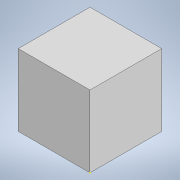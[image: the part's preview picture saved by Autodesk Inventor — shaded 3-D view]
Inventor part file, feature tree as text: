
AUTODESK INVENTOR PART (.ipt)
format: ipt  version: 2021 (Build 250183000, 183)  size: 107,520 bytes
history: native  units: in
note: dims shown in document units (in); Inventor stores cm internally (conversion verified against a paired STEP export)
features: sketch x3, extrude x2
ambient origin geometry x8: Origin, YZ Plane, XZ Plane, XY Plane, X Axis, Y Axis, Z Axis, Center Point
bodies: Solid1 (feature_tree)
feature tree (5):
  sketch  "Sketch1"  dims[d1=0.6299in d2=0.6299in]
  extrude  "Extrusion1"  Depth=0.6299in
  extrude  "Extrusion2"  Depth=0.5118in TaperAngle=0.0deg
  sketch  "Sketch2"  dims[d8=0.6299in d9=0.0in d18=0.5118in d19=0.0in]
  sketch  "Sketch3"  dims[d22=0.5118in d23=0.1417in d25=0.0709in d26=0.5118in d27=0.1417in]
